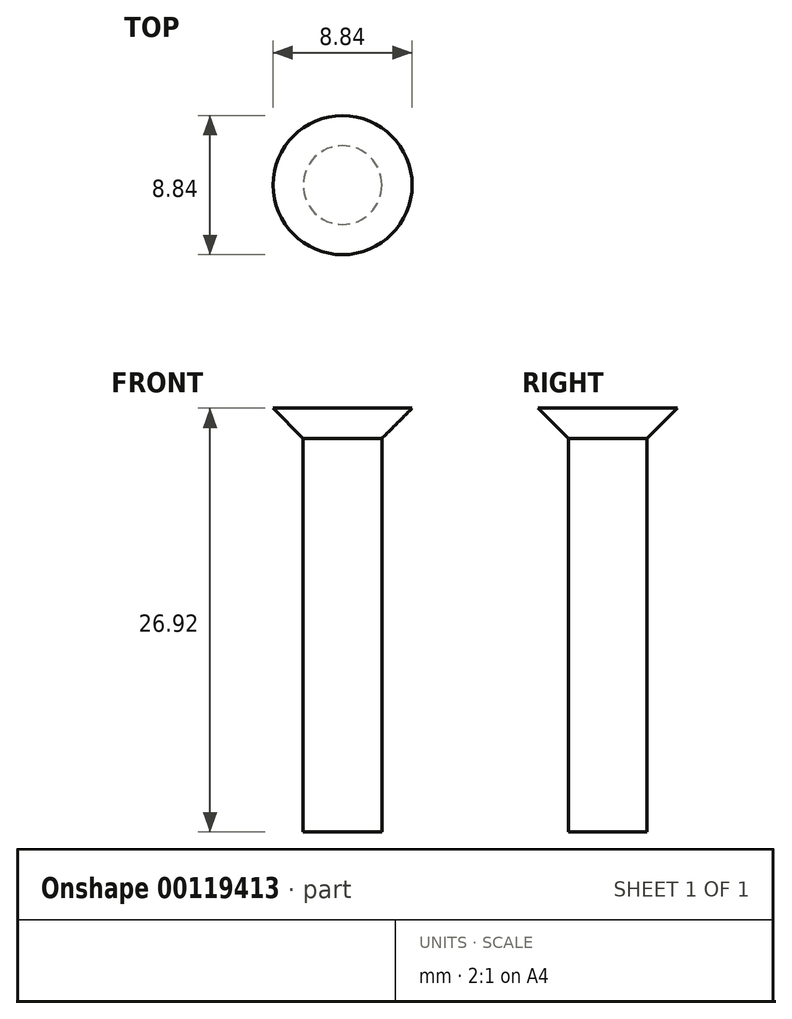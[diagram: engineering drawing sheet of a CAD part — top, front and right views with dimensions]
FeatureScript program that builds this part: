
annotation { "Feature Type Name" : "Feature", "Feature Type Description" : "" }
export const myFeature = defineFeature(function(context is Context, id is Id, definition is map)
    precondition{}
    {
        {
            var Q0;
            Q0=qCreatedBy(makeId("Front.planeOp"),FACE);
            var sketch = newSketch(context, id + "F0", { "sketchPlane" : qUnion([Q0])});
            skLineSegment(sketch, "E0", {"start": v(0, 28.51) * mm, "end": v(0, -10.66) * mm, "construction": true});
            skLineSegment(sketch, "E1.top", {"start": v(0, -4.55) * mm, "end": v(-2.5, -4.55) * mm});
            skLineSegment(sketch, "E1.right", {"start": v(-2.5, 20.45) * mm, "end": v(-2.5, -4.55) * mm});
            skLineSegment(sketch, "E2", {"start": v(-2.5, 20.45) * mm, "end": v(-4.42, 22.37) * mm});
            skLineSegment(sketch, "E3", {"start": v(-4.42, 22.37) * mm, "end": v(0, 22.37) * mm});
            skLineSegment(sketch, "E4", {"start": v(0, 22.37) * mm, "end": v(0, -4.55) * mm});
            skSolve(sketch);
        }
        {
            var Q0;
            Q0 = qSketchRegion(id + "F0", true);
            var Q1;
            Q1=sQuery(id+"F0.wireOp",EDGE,"E0");
            revolve(context, id + "F1", {"entities" : qUnion([Q0]), "axis" : qUnion([Q1]), "revolveType" : RevolveType.FULL});
        }
    });
